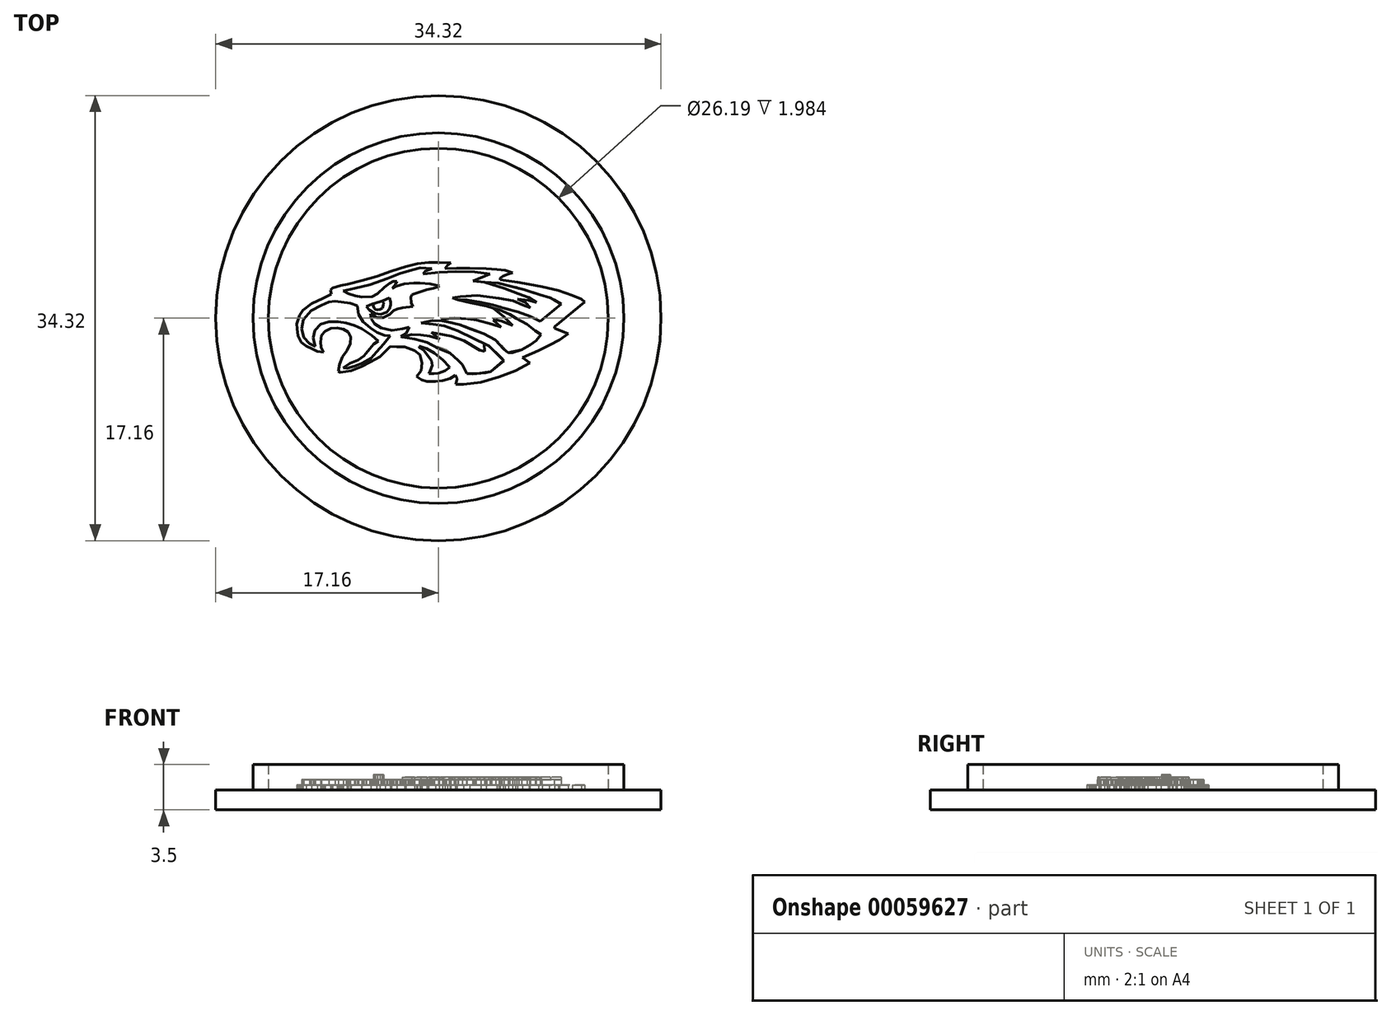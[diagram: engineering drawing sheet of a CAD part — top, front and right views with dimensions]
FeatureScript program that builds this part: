
annotation { "Feature Type Name" : "Feature", "Feature Type Description" : "" }
export const myFeature = defineFeature(function(context is Context, id is Id, definition is map)
    precondition{}
    {
        {
            var Q0;
            Q0=qCreatedBy(makeId("Top.planeOp"),FACE);
            var sketch = newSketch(context, id + "F0", { "sketchPlane" : qUnion([Q0])});
            skCircle(sketch, "E0", {"center": v(0, 0) * mm, "radius": 13.1 * mm});
            skSolve(sketch);
        }
        {
            var Q0;
            Q0=makeQuery(id+"F0.imprint","IMPRINT",FACE,{"disambiguationData":[TD([[makeQuery(id+"F0.imprint","IMPRINT",EDGE,{"derivedFrom":sQuery(id+"F0.wireOp",EDGE,"E0")}),1.0]])]});
            var sketch = newSketch(context, id + "F1", { "sketchPlane" : qUnion([Q0])});
            skLineSegment(sketch, "E1", {"start": v(-8.25, 1.86) * mm, "end": v(-8.31, 2.16) * mm});
            skLineSegment(sketch, "E2", {"start": v(-8.31, 2.16) * mm, "end": v(-8.17, 2.34) * mm});
            skLineSegment(sketch, "E3", {"start": v(-8.17, 2.34) * mm, "end": v(-7.5, 2.52) * mm});
            skLineSegment(sketch, "E4", {"start": v(-7.5, 2.52) * mm, "end": v(-7.03, 2.61) * mm});
            skLineSegment(sketch, "E5", {"start": v(-7.03, 2.61) * mm, "end": v(-5.88, 2.9) * mm});
            skLineSegment(sketch, "E6", {"start": v(-5.88, 2.9) * mm, "end": v(-4.76, 3.23) * mm});
            skLineSegment(sketch, "E7", {"start": v(-4.76, 3.23) * mm, "end": v(-3.62, 3.64) * mm});
            skLineSegment(sketch, "E8", {"start": v(-3.62, 3.64) * mm, "end": v(-2.5, 3.98) * mm});
            skLineSegment(sketch, "E9", {"start": v(-2.5, 3.98) * mm, "end": v(-1.62, 4.19) * mm});
            skLineSegment(sketch, "E10", {"start": v(-1.62, 4.19) * mm, "end": v(-0.77, 4.29) * mm});
            skLineSegment(sketch, "E11", {"start": v(-0.77, 4.29) * mm, "end": v(0.08, 4.3) * mm});
            skLineSegment(sketch, "E12", {"start": v(0.08, 4.3) * mm, "end": v(0.97, 4.25) * mm});
            skLineSegment(sketch, "E13", {"start": v(0.97, 4.25) * mm, "end": v(0.7, 4.06) * mm});
            skLineSegment(sketch, "E14", {"start": v(0.7, 4.06) * mm, "end": v(0.52, 3.84) * mm});
            skLineSegment(sketch, "E15", {"start": v(1.4, 3.85) * mm, "end": v(0.52, 3.84) * mm});
            skLineSegment(sketch, "E16", {"start": v(2.43, 3.85) * mm, "end": v(1.4, 3.85) * mm});
            skLineSegment(sketch, "E17", {"start": v(2.43, 3.85) * mm, "end": v(3.68, 3.82) * mm});
            skLineSegment(sketch, "E18", {"start": v(3.68, 3.82) * mm, "end": v(4.52, 3.76) * mm});
            skLineSegment(sketch, "E19", {"start": v(4.52, 3.76) * mm, "end": v(5.15, 3.7) * mm});
            skLineSegment(sketch, "E20", {"start": v(5.15, 3.7) * mm, "end": v(5.73, 3.51) * mm});
            skLineSegment(sketch, "E21", {"start": v(5.73, 3.51) * mm, "end": v(5.42, 3.4) * mm});
            skLineSegment(sketch, "E22", {"start": v(5.42, 3.4) * mm, "end": v(4.99, 3.26) * mm});
            skLineSegment(sketch, "E23", {"start": v(4.99, 3.26) * mm, "end": v(4.78, 3.1) * mm});
            skLineSegment(sketch, "E24", {"start": v(4.78, 3.1) * mm, "end": v(4.76, 2.97) * mm});
            skLineSegment(sketch, "E25", {"start": v(4.76, 2.97) * mm, "end": v(6.1, 2.76) * mm});
            skLineSegment(sketch, "E26", {"start": v(6.1, 2.76) * mm, "end": v(6.98, 2.63) * mm});
            skLineSegment(sketch, "E27", {"start": v(6.98, 2.63) * mm, "end": v(8, 2.44) * mm});
            skLineSegment(sketch, "E28", {"start": v(8, 2.44) * mm, "end": v(9.23, 2.15) * mm});
            skLineSegment(sketch, "E29", {"start": v(9.23, 2.15) * mm, "end": v(10.32, 1.76) * mm});
            skLineSegment(sketch, "E30", {"start": v(10.32, 1.76) * mm, "end": v(11.02, 1.46) * mm});
            skLineSegment(sketch, "E31", {"start": v(11.02, 1.46) * mm, "end": v(11.27, 1.26) * mm});
            skLineSegment(sketch, "E32", {"start": v(11.27, 1.26) * mm, "end": v(8.96, -0.67) * mm});
            skLineSegment(sketch, "E33", {"start": v(8.96, -0.67) * mm, "end": v(8.96, -0.78) * mm});
            skLineSegment(sketch, "E34", {"start": v(8.96, -0.78) * mm, "end": v(10, -1.18) * mm});
            skLineSegment(sketch, "E35", {"start": v(10, -1.18) * mm, "end": v(9.34, -1.68) * mm});
            skLineSegment(sketch, "E36", {"start": v(9.34, -1.68) * mm, "end": v(8.56, -2.1) * mm});
            skLineSegment(sketch, "E37", {"start": v(8.56, -2.1) * mm, "end": v(7.72, -2.5) * mm});
            skLineSegment(sketch, "E38", {"start": v(7.72, -2.5) * mm, "end": v(6.48, -3.05) * mm});
            skLineSegment(sketch, "E39", {"start": v(6.48, -3.05) * mm, "end": v(7.04, -3.45) * mm});
            skLineSegment(sketch, "E40", {"start": v(7.04, -3.45) * mm, "end": v(5.93, -4.04) * mm});
            skLineSegment(sketch, "E41", {"start": v(5.93, -4.04) * mm, "end": v(4.68, -4.54) * mm});
            skLineSegment(sketch, "E42", {"start": v(4.68, -4.54) * mm, "end": v(3.27, -4.94) * mm});
            skLineSegment(sketch, "E43", {"start": v(3.27, -4.94) * mm, "end": v(1.95, -5.1) * mm});
            skLineSegment(sketch, "E44", {"start": v(1.95, -5.1) * mm, "end": v(1.35, -5.1) * mm});
            skLineSegment(sketch, "E45", {"start": v(1.35, -5.1) * mm, "end": v(1.45, -4.73) * mm});
            skLineSegment(sketch, "E46", {"start": v(1.45, -4.73) * mm, "end": v(1.4, -4.53) * mm});
            skLineSegment(sketch, "E47", {"start": v(1.4, -4.53) * mm, "end": v(1.3, -4.41) * mm});
            skLineSegment(sketch, "E48", {"start": v(1.3, -4.41) * mm, "end": v(0.9, -4.65) * mm});
            skLineSegment(sketch, "E49", {"start": v(0.9, -4.65) * mm, "end": v(0.32, -4.83) * mm});
            skLineSegment(sketch, "E50", {"start": v(0.32, -4.83) * mm, "end": v(-0.22, -4.88) * mm});
            skLineSegment(sketch, "E51", {"start": v(-0.22, -4.88) * mm, "end": v(-0.88, -4.86) * mm});
            skLineSegment(sketch, "E52", {"start": v(-0.88, -4.86) * mm, "end": v(-1.29, -4.75) * mm});
            skLineSegment(sketch, "E53", {"start": v(-1.29, -4.75) * mm, "end": v(-1.67, -4.5) * mm});
            skLineSegment(sketch, "E54", {"start": v(-1.67, -4.5) * mm, "end": v(-1.33, -4.06) * mm});
            skLineSegment(sketch, "E55", {"start": v(-1.33, -4.06) * mm, "end": v(-1.25, -3.45) * mm});
            skLineSegment(sketch, "E56", {"start": v(-1.25, -3.45) * mm, "end": v(-1.43, -2.82) * mm});
            skLineSegment(sketch, "E57", {"start": v(-1.43, -2.82) * mm, "end": v(-1.83, -2.5) * mm});
            skLineSegment(sketch, "E58", {"start": v(-1.83, -2.5) * mm, "end": v(-2.59, -2.2) * mm});
            skLineSegment(sketch, "E59", {"start": v(-2.59, -2.2) * mm, "end": v(-3.2, -2.23) * mm});
            skLineSegment(sketch, "E60", {"start": v(-3.2, -2.23) * mm, "end": v(-3.71, -2.18) * mm});
            skLineSegment(sketch, "E61", {"start": v(-3.71, -2.18) * mm, "end": v(-4.08, -2.56) * mm});
            skLineSegment(sketch, "E62", {"start": v(-4.08, -2.56) * mm, "end": v(-4.52, -2.97) * mm});
            skLineSegment(sketch, "E63", {"start": v(-4.52, -2.97) * mm, "end": v(-5.2, -3.37) * mm});
            skLineSegment(sketch, "E64", {"start": v(-5.2, -3.37) * mm, "end": v(-5.93, -3.74) * mm});
            skLineSegment(sketch, "E65", {"start": v(-5.93, -3.74) * mm, "end": v(-6.74, -4.06) * mm});
            skLineSegment(sketch, "E66", {"start": v(-6.74, -4.06) * mm, "end": v(-7.54, -4.19) * mm});
            skLineSegment(sketch, "E67", {"start": v(-7.54, -4.19) * mm, "end": v(-7.72, -4.07) * mm});
            skLineSegment(sketch, "E68", {"start": v(-7.72, -4.07) * mm, "end": v(-7.6, -3.54) * mm});
            skLineSegment(sketch, "E69", {"start": v(-7.6, -3.54) * mm, "end": v(-7.4, -2.97) * mm});
            skLineSegment(sketch, "E70", {"start": v(-7.4, -2.97) * mm, "end": v(-7.04, -2.48) * mm});
            skLineSegment(sketch, "E71", {"start": v(-7.04, -2.48) * mm, "end": v(-6.78, -1.95) * mm});
            skLineSegment(sketch, "E72", {"start": v(-6.78, -1.95) * mm, "end": v(-6.77, -1.45) * mm});
            skLineSegment(sketch, "E73", {"start": v(-6.77, -1.45) * mm, "end": v(-6.95, -1.08) * mm});
            skLineSegment(sketch, "E74", {"start": v(-6.95, -1.08) * mm, "end": v(-7.32, -0.86) * mm});
            skLineSegment(sketch, "E75", {"start": v(-7.32, -0.86) * mm, "end": v(-7.8, -0.75) * mm});
            skLineSegment(sketch, "E76", {"start": v(-7.8, -0.75) * mm, "end": v(-8.28, -0.8) * mm});
            skLineSegment(sketch, "E77", {"start": v(-8.28, -0.8) * mm, "end": v(-8.73, -1) * mm});
            skLineSegment(sketch, "E78", {"start": v(-8.73, -1) * mm, "end": v(-9, -1.33) * mm});
            skLineSegment(sketch, "E79", {"start": v(-9, -1.33) * mm, "end": v(-9.08, -1.82) * mm});
            skLineSegment(sketch, "E80", {"start": v(-9.08, -1.82) * mm, "end": v(-9.04, -2.24) * mm});
            skLineSegment(sketch, "E81", {"start": v(-9.04, -2.24) * mm, "end": v(-8.84, -2.61) * mm});
            skLineSegment(sketch, "E82", {"start": v(-8.84, -2.61) * mm, "end": v(-9.32, -2.55) * mm});
            skLineSegment(sketch, "E83", {"start": v(-9.32, -2.55) * mm, "end": v(-9.71, -2.37) * mm});
            skLineSegment(sketch, "E84", {"start": v(-9.71, -2.37) * mm, "end": v(-10.18, -2.16) * mm});
            skLineSegment(sketch, "E85", {"start": v(-10.18, -2.16) * mm, "end": v(-10.58, -1.87) * mm});
            skLineSegment(sketch, "E86", {"start": v(-10.58, -1.87) * mm, "end": v(-10.82, -1.36) * mm});
            skLineSegment(sketch, "E87", {"start": v(-10.82, -1.36) * mm, "end": v(-10.9, -0.83) * mm});
            skLineSegment(sketch, "E88", {"start": v(-10.9, -0.83) * mm, "end": v(-10.92, -0.42) * mm});
            skLineSegment(sketch, "E89", {"start": v(-10.92, -0.42) * mm, "end": v(-10.7, 0.22) * mm});
            skLineSegment(sketch, "E90", {"start": v(-10.7, 0.22) * mm, "end": v(-10.43, 0.6) * mm});
            skLineSegment(sketch, "E91", {"start": v(-10.43, 0.6) * mm, "end": v(-9.76, 1.13) * mm});
            skLineSegment(sketch, "E92", {"start": v(-9.76, 1.13) * mm, "end": v(-8.9, 1.52) * mm});
            skLineSegment(sketch, "E93", {"start": v(-8.9, 1.52) * mm, "end": v(-8.25, 1.86) * mm});
            skSolve(sketch);
        }
        {
            var Q0;
            Q0 = qSketchRegion(id + "F1", true);
            extrude(context, id + "F2", {"entities" : qUnion([Q0]), "depth" : 0.4 * mm});
        }
        {
            var Q0;
            Q0=makeQuery(id+"F2.opExtrude","CAP_FACE",FACE,{"disambiguationData":[OSD([sQuery(id+"F1.wireOp",EDGE,"E1"),sQuery(id+"F1.wireOp",EDGE,"E2"),sQuery(id+"F1.wireOp",EDGE,"E3"),sQuery(id+"F1.wireOp",EDGE,"E4"),sQuery(id+"F1.wireOp",EDGE,"E5"),sQuery(id+"F1.wireOp",EDGE,"E6"),sQuery(id+"F1.wireOp",EDGE,"E7"),sQuery(id+"F1.wireOp",EDGE,"E8"),sQuery(id+"F1.wireOp",EDGE,"E9"),sQuery(id+"F1.wireOp",EDGE,"E10"),sQuery(id+"F1.wireOp",EDGE,"E11"),sQuery(id+"F1.wireOp",EDGE,"E12"),sQuery(id+"F1.wireOp",EDGE,"E13"),sQuery(id+"F1.wireOp",EDGE,"E14"),sQuery(id+"F1.wireOp",EDGE,"E15"),sQuery(id+"F1.wireOp",EDGE,"E16"),sQuery(id+"F1.wireOp",EDGE,"E17"),sQuery(id+"F1.wireOp",EDGE,"E18"),sQuery(id+"F1.wireOp",EDGE,"E19"),sQuery(id+"F1.wireOp",EDGE,"E20"),sQuery(id+"F1.wireOp",EDGE,"E21"),sQuery(id+"F1.wireOp",EDGE,"E22"),sQuery(id+"F1.wireOp",EDGE,"E23"),sQuery(id+"F1.wireOp",EDGE,"E24"),sQuery(id+"F1.wireOp",EDGE,"E25"),sQuery(id+"F1.wireOp",EDGE,"E26"),sQuery(id+"F1.wireOp",EDGE,"E27"),sQuery(id+"F1.wireOp",EDGE,"E28"),sQuery(id+"F1.wireOp",EDGE,"E29"),sQuery(id+"F1.wireOp",EDGE,"E30"),sQuery(id+"F1.wireOp",EDGE,"E31"),sQuery(id+"F1.wireOp",EDGE,"E32"),sQuery(id+"F1.wireOp",EDGE,"E33"),sQuery(id+"F1.wireOp",EDGE,"E34"),sQuery(id+"F1.wireOp",EDGE,"E35"),sQuery(id+"F1.wireOp",EDGE,"E36"),sQuery(id+"F1.wireOp",EDGE,"E37"),sQuery(id+"F1.wireOp",EDGE,"E38"),sQuery(id+"F1.wireOp",EDGE,"E39"),sQuery(id+"F1.wireOp",EDGE,"E40"),sQuery(id+"F1.wireOp",EDGE,"E41"),sQuery(id+"F1.wireOp",EDGE,"E42"),sQuery(id+"F1.wireOp",EDGE,"E43"),sQuery(id+"F1.wireOp",EDGE,"E44"),sQuery(id+"F1.wireOp",EDGE,"E45"),sQuery(id+"F1.wireOp",EDGE,"E46"),sQuery(id+"F1.wireOp",EDGE,"E47"),sQuery(id+"F1.wireOp",EDGE,"E48"),sQuery(id+"F1.wireOp",EDGE,"E49"),sQuery(id+"F1.wireOp",EDGE,"E50"),sQuery(id+"F1.wireOp",EDGE,"E51"),sQuery(id+"F1.wireOp",EDGE,"E52"),sQuery(id+"F1.wireOp",EDGE,"E53"),sQuery(id+"F1.wireOp",EDGE,"E54"),sQuery(id+"F1.wireOp",EDGE,"E55"),sQuery(id+"F1.wireOp",EDGE,"E56"),sQuery(id+"F1.wireOp",EDGE,"E57"),sQuery(id+"F1.wireOp",EDGE,"E58"),sQuery(id+"F1.wireOp",EDGE,"E59"),sQuery(id+"F1.wireOp",EDGE,"E60"),sQuery(id+"F1.wireOp",EDGE,"E61"),sQuery(id+"F1.wireOp",EDGE,"E62"),sQuery(id+"F1.wireOp",EDGE,"E63"),sQuery(id+"F1.wireOp",EDGE,"E64"),sQuery(id+"F1.wireOp",EDGE,"E65"),sQuery(id+"F1.wireOp",EDGE,"E66"),sQuery(id+"F1.wireOp",EDGE,"E67"),sQuery(id+"F1.wireOp",EDGE,"E68"),sQuery(id+"F1.wireOp",EDGE,"E69"),sQuery(id+"F1.wireOp",EDGE,"E70"),sQuery(id+"F1.wireOp",EDGE,"E71"),sQuery(id+"F1.wireOp",EDGE,"E72"),sQuery(id+"F1.wireOp",EDGE,"E73"),sQuery(id+"F1.wireOp",EDGE,"E74"),sQuery(id+"F1.wireOp",EDGE,"E75"),sQuery(id+"F1.wireOp",EDGE,"E76"),sQuery(id+"F1.wireOp",EDGE,"E77"),sQuery(id+"F1.wireOp",EDGE,"E78"),sQuery(id+"F1.wireOp",EDGE,"E79"),sQuery(id+"F1.wireOp",EDGE,"E80"),sQuery(id+"F1.wireOp",EDGE,"E81"),sQuery(id+"F1.wireOp",EDGE,"E82"),sQuery(id+"F1.wireOp",EDGE,"E83"),sQuery(id+"F1.wireOp",EDGE,"E84"),sQuery(id+"F1.wireOp",EDGE,"E85"),sQuery(id+"F1.wireOp",EDGE,"E86"),sQuery(id+"F1.wireOp",EDGE,"E87"),sQuery(id+"F1.wireOp",EDGE,"E88"),sQuery(id+"F1.wireOp",EDGE,"E89"),sQuery(id+"F1.wireOp",EDGE,"E90"),sQuery(id+"F1.wireOp",EDGE,"E91"),sQuery(id+"F1.wireOp",EDGE,"E92"),sQuery(id+"F1.wireOp",EDGE,"E93")])],"isStart":false});
            var sketch = newSketch(context, id + "F3", { "sketchPlane" : qUnion([Q0])});
            skLineSegment(sketch, "E94", {"start": v(-7.32, 2.1) * mm, "end": v(-6.48, 2.29) * mm});
            skLineSegment(sketch, "E95", {"start": v(-6.48, 2.29) * mm, "end": v(-5.26, 2.57) * mm});
            skLineSegment(sketch, "E96", {"start": v(-5.26, 2.57) * mm, "end": v(-3.95, 3.07) * mm});
            skLineSegment(sketch, "E97", {"start": v(-3.95, 3.07) * mm, "end": v(-2.99, 3.44) * mm});
            skLineSegment(sketch, "E98", {"start": v(-2.99, 3.44) * mm, "end": v(-2, 3.71) * mm});
            skLineSegment(sketch, "E99", {"start": v(-2, 3.71) * mm, "end": v(-1.4, 3.9) * mm});
            skLineSegment(sketch, "E100", {"start": v(-1.4, 3.9) * mm, "end": v(-0.51, 3.81) * mm});
            skLineSegment(sketch, "E101", {"start": v(-0.51, 3.81) * mm, "end": v(-1, 3.63) * mm});
            skLineSegment(sketch, "E102", {"start": v(-1, 3.63) * mm, "end": v(-1.18, 3.42) * mm});
            skLineSegment(sketch, "E103", {"start": v(-1.18, 3.42) * mm, "end": v(0.05, 3.55) * mm});
            skLineSegment(sketch, "E104", {"start": v(0.05, 3.55) * mm, "end": v(1.33, 3.6) * mm});
            skLineSegment(sketch, "E105", {"start": v(1.33, 3.6) * mm, "end": v(2.79, 3.58) * mm});
            skLineSegment(sketch, "E106", {"start": v(2.79, 3.58) * mm, "end": v(3.97, 3.41) * mm});
            skLineSegment(sketch, "E107", {"start": v(3.97, 3.41) * mm, "end": v(2.68, 2.85) * mm});
            skLineSegment(sketch, "E108", {"start": v(2.68, 2.85) * mm, "end": v(3.57, 2.77) * mm});
            skLineSegment(sketch, "E109", {"start": v(3.57, 2.77) * mm, "end": v(4.83, 2.6) * mm});
            skLineSegment(sketch, "E110", {"start": v(4.83, 2.6) * mm, "end": v(6.03, 2.36) * mm});
            skLineSegment(sketch, "E111", {"start": v(6.03, 2.36) * mm, "end": v(7.1, 2.05) * mm});
            skLineSegment(sketch, "E112", {"start": v(7.1, 2.05) * mm, "end": v(7.96, 1.76) * mm});
            skLineSegment(sketch, "E113", {"start": v(7.96, 1.76) * mm, "end": v(8.91, 1.42) * mm});
            skLineSegment(sketch, "E114", {"start": v(8.91, 1.42) * mm, "end": v(9.48, 1.1) * mm});
            skLineSegment(sketch, "E115", {"start": v(9.48, 1.1) * mm, "end": v(7.85, -0.25) * mm});
            skLineSegment(sketch, "E116", {"start": v(7.85, -0.25) * mm, "end": v(7.03, 0.17) * mm});
            skLineSegment(sketch, "E117", {"start": v(7.03, 0.17) * mm, "end": v(5.88, 0.57) * mm});
            skLineSegment(sketch, "E118", {"start": v(5.88, 0.57) * mm, "end": v(4.83, 0.9) * mm});
            skLineSegment(sketch, "E119", {"start": v(4.83, 0.9) * mm, "end": v(3.56, 1.16) * mm});
            skLineSegment(sketch, "E120", {"start": v(3.56, 1.16) * mm, "end": v(2.72, 1.3) * mm});
            skLineSegment(sketch, "E121", {"start": v(2.72, 1.3) * mm, "end": v(2.2, 1.41) * mm});
            skLineSegment(sketch, "E122", {"start": v(2.2, 1.41) * mm, "end": v(1.52, 1.42) * mm});
            skLineSegment(sketch, "E123", {"start": v(1.52, 1.42) * mm, "end": v(2.49, 1.2) * mm});
            skLineSegment(sketch, "E124", {"start": v(2.49, 1.2) * mm, "end": v(3.72, 0.92) * mm});
            skLineSegment(sketch, "E125", {"start": v(3.72, 0.92) * mm, "end": v(4.72, 0.64) * mm});
            skLineSegment(sketch, "E126", {"start": v(4.72, 0.64) * mm, "end": v(5.5, 0.29) * mm});
            skLineSegment(sketch, "E127", {"start": v(5.5, 0.29) * mm, "end": v(6.21, -0.14) * mm});
            skLineSegment(sketch, "E128", {"start": v(6.21, -0.14) * mm, "end": v(6.82, -0.48) * mm});
            skLineSegment(sketch, "E129", {"start": v(6.82, -0.48) * mm, "end": v(7.45, -0.99) * mm});
            skLineSegment(sketch, "E130", {"start": v(7.45, -0.99) * mm, "end": v(7.9, -1.27) * mm});
            skLineSegment(sketch, "E131", {"start": v(7.9, -1.27) * mm, "end": v(7.54, -1.7) * mm});
            skLineSegment(sketch, "E132", {"start": v(7.54, -1.7) * mm, "end": v(7.08, -2.04) * mm});
            skLineSegment(sketch, "E133", {"start": v(7.08, -2.04) * mm, "end": v(6.42, -2.43) * mm});
            skLineSegment(sketch, "E134", {"start": v(6.42, -2.43) * mm, "end": v(5.72, -2.65) * mm});
            skLineSegment(sketch, "E135", {"start": v(5.72, -2.65) * mm, "end": v(5.38, -2.64) * mm});
            skLineSegment(sketch, "E136", {"start": v(5.38, -2.64) * mm, "end": v(4.68, -1.86) * mm});
            skLineSegment(sketch, "E137", {"start": v(4.68, -1.86) * mm, "end": v(4.11, -1.5) * mm});
            skLineSegment(sketch, "E138", {"start": v(4.11, -1.5) * mm, "end": v(2.89, -0.92) * mm});
            skLineSegment(sketch, "E139", {"start": v(2.89, -0.92) * mm, "end": v(2.16, -0.64) * mm});
            skLineSegment(sketch, "E140", {"start": v(2.16, -0.64) * mm, "end": v(0.95, -0.34) * mm});
            skLineSegment(sketch, "E141", {"start": v(0.95, -0.34) * mm, "end": v(0.3, -0.2) * mm});
            skLineSegment(sketch, "E142", {"start": v(0.3, -0.2) * mm, "end": v(-0.44, -0.19) * mm});
            skLineSegment(sketch, "E143", {"start": v(-0.44, -0.19) * mm, "end": v(-1.33, -0.36) * mm});
            skLineSegment(sketch, "E144", {"start": v(-1.33, -0.36) * mm, "end": v(-0.42, -0.46) * mm});
            skLineSegment(sketch, "E145", {"start": v(-0.42, -0.46) * mm, "end": v(0.45, -0.59) * mm});
            skLineSegment(sketch, "E146", {"start": v(0.45, -0.59) * mm, "end": v(1.5, -0.98) * mm});
            skLineSegment(sketch, "E147", {"start": v(1.5, -0.98) * mm, "end": v(2.74, -1.58) * mm});
            skLineSegment(sketch, "E148", {"start": v(2.74, -1.58) * mm, "end": v(3.74, -2.07) * mm});
            skLineSegment(sketch, "E149", {"start": v(3.74, -2.07) * mm, "end": v(4.43, -2.63) * mm});
            skLineSegment(sketch, "E150", {"start": v(4.43, -2.63) * mm, "end": v(4.89, -3.1) * mm});
            skLineSegment(sketch, "E151", {"start": v(4.89, -3.1) * mm, "end": v(5.05, -3.28) * mm});
            skLineSegment(sketch, "E152", {"start": v(5.05, -3.28) * mm, "end": v(4.02, -4.12) * mm});
            skLineSegment(sketch, "E153", {"start": v(4.02, -4.12) * mm, "end": v(3.63, -4.2) * mm});
            skLineSegment(sketch, "E154", {"start": v(3.63, -4.2) * mm, "end": v(3.26, -4.23) * mm});
            skLineSegment(sketch, "E155", {"start": v(3.26, -4.23) * mm, "end": v(2.63, -4.3) * mm});
            skLineSegment(sketch, "E156", {"start": v(2.63, -4.3) * mm, "end": v(2.2, -4.26) * mm});
            skLineSegment(sketch, "E157", {"start": v(2.2, -4.26) * mm, "end": v(1.84, -3.58) * mm});
            skLineSegment(sketch, "E158", {"start": v(1.84, -3.58) * mm, "end": v(1.22, -2.94) * mm});
            skLineSegment(sketch, "E159", {"start": v(1.22, -2.94) * mm, "end": v(0.6, -2.45) * mm});
            skLineSegment(sketch, "E160", {"start": v(0.6, -2.45) * mm, "end": v(-1.24, -1.72) * mm});
            skLineSegment(sketch, "E161", {"start": v(-1.24, -1.72) * mm, "end": v(-1.83, -1.6) * mm});
            skLineSegment(sketch, "E162", {"start": v(-1.83, -1.6) * mm, "end": v(-2.8, -1.43) * mm});
            skLineSegment(sketch, "E163", {"start": v(-2.8, -1.43) * mm, "end": v(-2.9, -1.43) * mm});
            skLineSegment(sketch, "E164", {"start": v(-2.9, -1.43) * mm, "end": v(-2.52, -1.18) * mm});
            skLineSegment(sketch, "E165", {"start": v(-2.52, -1.18) * mm, "end": v(-2.35, -0.9) * mm});
            skLineSegment(sketch, "E166", {"start": v(-2.35, -0.9) * mm, "end": v(-2.25, -0.69) * mm});
            skLineSegment(sketch, "E167", {"start": v(-2.25, -0.69) * mm, "end": v(-2.76, -0.82) * mm});
            skLineSegment(sketch, "E168", {"start": v(-2.76, -0.82) * mm, "end": v(-3.58, -0.95) * mm});
            skLineSegment(sketch, "E169", {"start": v(-3.58, -0.95) * mm, "end": v(-4.42, -0.76) * mm});
            skLineSegment(sketch, "E170", {"start": v(-4.42, -0.76) * mm, "end": v(-4.92, -0.45) * mm});
            skLineSegment(sketch, "E171", {"start": v(-4.92, -0.45) * mm, "end": v(-5.17, -0.04) * mm});
            skLineSegment(sketch, "E172", {"start": v(-5.17, -0.04) * mm, "end": v(-5.22, 0.33) * mm});
            skLineSegment(sketch, "E173", {"start": v(-5.22, 0.33) * mm, "end": v(-4.77, 0.05) * mm});
            skLineSegment(sketch, "E174", {"start": v(-4.77, 0.05) * mm, "end": v(-4.25, 0.04) * mm});
            skLineSegment(sketch, "E175", {"start": v(-4.25, 0.04) * mm, "end": v(-3.75, 0.3) * mm});
            skLineSegment(sketch, "E176", {"start": v(-3.75, 0.3) * mm, "end": v(-3.45, 0.58) * mm});
            skLineSegment(sketch, "E177", {"start": v(-3.45, 0.58) * mm, "end": v(-3.16, 0.72) * mm});
            skLineSegment(sketch, "E178", {"start": v(-3.16, 0.72) * mm, "end": v(-2.74, 0.8) * mm});
            skLineSegment(sketch, "E179", {"start": v(-2.74, 0.8) * mm, "end": v(-1.95, 0.9) * mm});
            skLineSegment(sketch, "E180", {"start": v(-1.95, 0.9) * mm, "end": v(-2.09, 1.2) * mm});
            skLineSegment(sketch, "E181", {"start": v(-2.09, 1.2) * mm, "end": v(-2.12, 1.63) * mm});
            skLineSegment(sketch, "E182", {"start": v(-2.12, 1.63) * mm, "end": v(-2.03, 1.82) * mm});
            skLineSegment(sketch, "E183", {"start": v(-2.03, 1.82) * mm, "end": v(-1.37, 2.05) * mm});
            skLineSegment(sketch, "E184", {"start": v(-1.37, 2.05) * mm, "end": v(-0.9, 2.2) * mm});
            skLineSegment(sketch, "E185", {"start": v(-0.9, 2.2) * mm, "end": v(-0.41, 2.31) * mm});
            skLineSegment(sketch, "E186", {"start": v(-0.41, 2.31) * mm, "end": v(0, 2.42) * mm});
            skLineSegment(sketch, "E187", {"start": v(0, 2.42) * mm, "end": v(0.06, 2.48) * mm});
            skLineSegment(sketch, "E188", {"start": v(0.06, 2.48) * mm, "end": v(-0.62, 2.65) * mm});
            skLineSegment(sketch, "E189", {"start": v(-0.62, 2.65) * mm, "end": v(-1.41, 2.72) * mm});
            skLineSegment(sketch, "E190", {"start": v(-1.41, 2.72) * mm, "end": v(-1.91, 2.73) * mm});
            skLineSegment(sketch, "E191", {"start": v(-1.91, 2.73) * mm, "end": v(-2.62, 2.64) * mm});
            skLineSegment(sketch, "E192", {"start": v(-2.62, 2.64) * mm, "end": v(-3.26, 2.44) * mm});
            skLineSegment(sketch, "E193", {"start": v(-3.26, 2.44) * mm, "end": v(-3.55, 2.29) * mm});
            skLineSegment(sketch, "E194", {"start": v(-3.55, 2.29) * mm, "end": v(-3.3, 2.62) * mm});
            skLineSegment(sketch, "E195", {"start": v(-3.3, 2.62) * mm, "end": v(-3.2, 2.84) * mm});
            skLineSegment(sketch, "E196", {"start": v(-3.2, 2.84) * mm, "end": v(-3.48, 2.85) * mm});
            skLineSegment(sketch, "E197", {"start": v(-3.48, 2.85) * mm, "end": v(-3.77, 2.68) * mm});
            skLineSegment(sketch, "E198", {"start": v(-3.77, 2.68) * mm, "end": v(-4.16, 2.38) * mm});
            skLineSegment(sketch, "E199", {"start": v(-4.16, 2.38) * mm, "end": v(-4.7, 1.89) * mm});
            skLineSegment(sketch, "E200", {"start": v(-4.7, 1.89) * mm, "end": v(-5.1, 1.67) * mm});
            skLineSegment(sketch, "E201", {"start": v(-5.1, 1.67) * mm, "end": v(-5.89, 1.63) * mm});
            skLineSegment(sketch, "E202", {"start": v(-5.89, 1.63) * mm, "end": v(-6.4, 1.72) * mm});
            skLineSegment(sketch, "E203", {"start": v(-6.4, 1.72) * mm, "end": v(-6.9, 1.88) * mm});
            skLineSegment(sketch, "E204", {"start": v(-6.9, 1.88) * mm, "end": v(-7.32, 2.1) * mm});
            skSolve(sketch);
        }
        {
            var Q0;
            Q0 = qSketchRegion(id + "F3", true);
            extrude(context, id + "F4", {"entities" : qUnion([Q0]), "operationType" : NewBodyOperationType.ADD, "depth" : 0.4 * mm});
        }
        {
            var Q0;
            Q0=makeQuery(id+"F2.opExtrude","CAP_FACE",FACE,{"disambiguationData":[OSD([sQuery(id+"F1.wireOp",EDGE,"E1"),sQuery(id+"F1.wireOp",EDGE,"E2"),sQuery(id+"F1.wireOp",EDGE,"E3"),sQuery(id+"F1.wireOp",EDGE,"E4"),sQuery(id+"F1.wireOp",EDGE,"E5"),sQuery(id+"F1.wireOp",EDGE,"E6"),sQuery(id+"F1.wireOp",EDGE,"E7"),sQuery(id+"F1.wireOp",EDGE,"E8"),sQuery(id+"F1.wireOp",EDGE,"E9"),sQuery(id+"F1.wireOp",EDGE,"E10"),sQuery(id+"F1.wireOp",EDGE,"E11"),sQuery(id+"F1.wireOp",EDGE,"E12"),sQuery(id+"F1.wireOp",EDGE,"E13"),sQuery(id+"F1.wireOp",EDGE,"E14"),sQuery(id+"F1.wireOp",EDGE,"E15"),sQuery(id+"F1.wireOp",EDGE,"E16"),sQuery(id+"F1.wireOp",EDGE,"E17"),sQuery(id+"F1.wireOp",EDGE,"E18"),sQuery(id+"F1.wireOp",EDGE,"E19"),sQuery(id+"F1.wireOp",EDGE,"E20"),sQuery(id+"F1.wireOp",EDGE,"E21"),sQuery(id+"F1.wireOp",EDGE,"E22"),sQuery(id+"F1.wireOp",EDGE,"E23"),sQuery(id+"F1.wireOp",EDGE,"E24"),sQuery(id+"F1.wireOp",EDGE,"E25"),sQuery(id+"F1.wireOp",EDGE,"E26"),sQuery(id+"F1.wireOp",EDGE,"E27"),sQuery(id+"F1.wireOp",EDGE,"E28"),sQuery(id+"F1.wireOp",EDGE,"E29"),sQuery(id+"F1.wireOp",EDGE,"E30"),sQuery(id+"F1.wireOp",EDGE,"E31"),sQuery(id+"F1.wireOp",EDGE,"E32"),sQuery(id+"F1.wireOp",EDGE,"E33"),sQuery(id+"F1.wireOp",EDGE,"E34"),sQuery(id+"F1.wireOp",EDGE,"E35"),sQuery(id+"F1.wireOp",EDGE,"E36"),sQuery(id+"F1.wireOp",EDGE,"E37"),sQuery(id+"F1.wireOp",EDGE,"E38"),sQuery(id+"F1.wireOp",EDGE,"E39"),sQuery(id+"F1.wireOp",EDGE,"E40"),sQuery(id+"F1.wireOp",EDGE,"E41"),sQuery(id+"F1.wireOp",EDGE,"E42"),sQuery(id+"F1.wireOp",EDGE,"E43"),sQuery(id+"F1.wireOp",EDGE,"E44"),sQuery(id+"F1.wireOp",EDGE,"E45"),sQuery(id+"F1.wireOp",EDGE,"E46"),sQuery(id+"F1.wireOp",EDGE,"E47"),sQuery(id+"F1.wireOp",EDGE,"E48"),sQuery(id+"F1.wireOp",EDGE,"E49"),sQuery(id+"F1.wireOp",EDGE,"E50"),sQuery(id+"F1.wireOp",EDGE,"E51"),sQuery(id+"F1.wireOp",EDGE,"E52"),sQuery(id+"F1.wireOp",EDGE,"E53"),sQuery(id+"F1.wireOp",EDGE,"E54"),sQuery(id+"F1.wireOp",EDGE,"E55"),sQuery(id+"F1.wireOp",EDGE,"E56"),sQuery(id+"F1.wireOp",EDGE,"E57"),sQuery(id+"F1.wireOp",EDGE,"E58"),sQuery(id+"F1.wireOp",EDGE,"E59"),sQuery(id+"F1.wireOp",EDGE,"E60"),sQuery(id+"F1.wireOp",EDGE,"E61"),sQuery(id+"F1.wireOp",EDGE,"E62"),sQuery(id+"F1.wireOp",EDGE,"E63"),sQuery(id+"F1.wireOp",EDGE,"E64"),sQuery(id+"F1.wireOp",EDGE,"E65"),sQuery(id+"F1.wireOp",EDGE,"E66"),sQuery(id+"F1.wireOp",EDGE,"E67"),sQuery(id+"F1.wireOp",EDGE,"E68"),sQuery(id+"F1.wireOp",EDGE,"E69"),sQuery(id+"F1.wireOp",EDGE,"E70"),sQuery(id+"F1.wireOp",EDGE,"E71"),sQuery(id+"F1.wireOp",EDGE,"E72"),sQuery(id+"F1.wireOp",EDGE,"E73"),sQuery(id+"F1.wireOp",EDGE,"E74"),sQuery(id+"F1.wireOp",EDGE,"E75"),sQuery(id+"F1.wireOp",EDGE,"E76"),sQuery(id+"F1.wireOp",EDGE,"E77"),sQuery(id+"F1.wireOp",EDGE,"E78"),sQuery(id+"F1.wireOp",EDGE,"E79"),sQuery(id+"F1.wireOp",EDGE,"E80"),sQuery(id+"F1.wireOp",EDGE,"E81"),sQuery(id+"F1.wireOp",EDGE,"E82"),sQuery(id+"F1.wireOp",EDGE,"E83"),sQuery(id+"F1.wireOp",EDGE,"E84"),sQuery(id+"F1.wireOp",EDGE,"E85"),sQuery(id+"F1.wireOp",EDGE,"E86"),sQuery(id+"F1.wireOp",EDGE,"E87"),sQuery(id+"F1.wireOp",EDGE,"E88"),sQuery(id+"F1.wireOp",EDGE,"E89"),sQuery(id+"F1.wireOp",EDGE,"E90"),sQuery(id+"F1.wireOp",EDGE,"E91"),sQuery(id+"F1.wireOp",EDGE,"E92"),sQuery(id+"F1.wireOp",EDGE,"E93")])],"isStart":false});
            var sketch = newSketch(context, id + "F5", { "sketchPlane" : qUnion([Q0])});
            skLineSegment(sketch, "E205", {"start": v(-1.5, -2.14) * mm, "end": v(-0.9, -2.32) * mm});
            skLineSegment(sketch, "E206", {"start": v(-0.9, -2.32) * mm, "end": v(-0.3, -2.67) * mm});
            skLineSegment(sketch, "E207", {"start": v(-0.3, -2.67) * mm, "end": v(0.37, -3.23) * mm});
            skLineSegment(sketch, "E208", {"start": v(0.37, -3.23) * mm, "end": v(0.84, -3.72) * mm});
            skLineSegment(sketch, "E209", {"start": v(0.84, -3.72) * mm, "end": v(0.87, -3.8) * mm});
            skLineSegment(sketch, "E210", {"start": v(0.87, -3.8) * mm, "end": v(0.52, -4.05) * mm});
            skLineSegment(sketch, "E211", {"start": v(0.52, -4.05) * mm, "end": v(0, -4.24) * mm});
            skLineSegment(sketch, "E212", {"start": v(0, -4.24) * mm, "end": v(-0.33, -4.28) * mm});
            skLineSegment(sketch, "E213", {"start": v(-0.33, -4.28) * mm, "end": v(-0.72, -4.27) * mm});
            skLineSegment(sketch, "E214", {"start": v(-0.72, -4.27) * mm, "end": v(-0.62, -4.04) * mm});
            skLineSegment(sketch, "E215", {"start": v(-0.62, -4.04) * mm, "end": v(-0.47, -3.64) * mm});
            skLineSegment(sketch, "E216", {"start": v(-0.47, -3.64) * mm, "end": v(-0.54, -3.26) * mm});
            skLineSegment(sketch, "E217", {"start": v(-0.54, -3.26) * mm, "end": v(-0.85, -2.85) * mm});
            skLineSegment(sketch, "E218", {"start": v(-0.85, -2.85) * mm, "end": v(-1.12, -2.5) * mm});
            skLineSegment(sketch, "E219", {"start": v(-1.12, -2.5) * mm, "end": v(-1.4, -2.3) * mm});
            skLineSegment(sketch, "E220", {"start": v(-1.4, -2.3) * mm, "end": v(-1.5, -2.14) * mm});
            skLineSegment(sketch, "E221", {"start": v(-9.5, -2.17) * mm, "end": v(-9.92, -1.94) * mm});
            skLineSegment(sketch, "E222", {"start": v(-9.92, -1.94) * mm, "end": v(-10.36, -1.47) * mm});
            skLineSegment(sketch, "E223", {"start": v(-10.36, -1.47) * mm, "end": v(-10.53, -0.82) * mm});
            skLineSegment(sketch, "E224", {"start": v(-10.53, -0.82) * mm, "end": v(-10.42, -0.12) * mm});
            skLineSegment(sketch, "E225", {"start": v(-10.42, -0.12) * mm, "end": v(-9.8, 0.58) * mm});
            skLineSegment(sketch, "E226", {"start": v(-9.8, 0.58) * mm, "end": v(-9.01, 1) * mm});
            skLineSegment(sketch, "E227", {"start": v(-9.01, 1) * mm, "end": v(-8.45, 1.26) * mm});
            skLineSegment(sketch, "E228", {"start": v(-8.45, 1.26) * mm, "end": v(-7.96, 1.32) * mm});
            skLineSegment(sketch, "E229", {"start": v(-7.96, 1.32) * mm, "end": v(-6.78, 1.17) * mm});
            skLineSegment(sketch, "E230", {"start": v(-6.78, 1.17) * mm, "end": v(-6.26, 0.95) * mm});
            skLineSegment(sketch, "E231", {"start": v(-6.26, 0.95) * mm, "end": v(-6.14, 0.3) * mm});
            skLineSegment(sketch, "E232", {"start": v(-6.14, 0.3) * mm, "end": v(-5.8, -0.27) * mm});
            skLineSegment(sketch, "E233", {"start": v(-5.8, -0.27) * mm, "end": v(-5.25, -0.76) * mm});
            skLineSegment(sketch, "E234", {"start": v(-5.25, -0.76) * mm, "end": v(-4.72, -1.1) * mm});
            skLineSegment(sketch, "E235", {"start": v(-4.72, -1.1) * mm, "end": v(-4.14, -1.3) * mm});
            skLineSegment(sketch, "E236", {"start": v(-4.14, -1.3) * mm, "end": v(-3.71, -1.35) * mm});
            skLineSegment(sketch, "E237", {"start": v(-3.71, -1.35) * mm, "end": v(-4.22, -1.97) * mm});
            skLineSegment(sketch, "E238", {"start": v(-4.22, -1.97) * mm, "end": v(-4.76, -2.6) * mm});
            skLineSegment(sketch, "E239", {"start": v(-4.76, -2.6) * mm, "end": v(-5.22, -3.1) * mm});
            skLineSegment(sketch, "E240", {"start": v(-5.22, -3.1) * mm, "end": v(-5.8, -3.45) * mm});
            skLineSegment(sketch, "E241", {"start": v(-5.8, -3.45) * mm, "end": v(-6.48, -3.69) * mm});
            skLineSegment(sketch, "E242", {"start": v(-6.48, -3.69) * mm, "end": v(-7.04, -3.86) * mm});
            skLineSegment(sketch, "E243", {"start": v(-7.04, -3.86) * mm, "end": v(-7.33, -3.84) * mm});
            skLineSegment(sketch, "E244", {"start": v(-7.33, -3.84) * mm, "end": v(-6.81, -3.5) * mm});
            skLineSegment(sketch, "E245", {"start": v(-6.81, -3.5) * mm, "end": v(-6.19, -3.22) * mm});
            skLineSegment(sketch, "E246", {"start": v(-6.19, -3.22) * mm, "end": v(-5.73, -2.92) * mm});
            skLineSegment(sketch, "E247", {"start": v(-5.73, -2.92) * mm, "end": v(-5.6, -2.73) * mm});
            skLineSegment(sketch, "E248", {"start": v(-5.6, -2.73) * mm, "end": v(-5.3, -2.37) * mm});
            skLineSegment(sketch, "E249", {"start": v(-5.3, -2.37) * mm, "end": v(-4.99, -2) * mm});
            skLineSegment(sketch, "E250", {"start": v(-4.99, -2) * mm, "end": v(-4.63, -1.78) * mm});
            skLineSegment(sketch, "E251", {"start": v(-4.63, -1.78) * mm, "end": v(-5.14, -1.3) * mm});
            skLineSegment(sketch, "E252", {"start": v(-5.14, -1.3) * mm, "end": v(-5.88, -0.8) * mm});
            skLineSegment(sketch, "E253", {"start": v(-5.88, -0.8) * mm, "end": v(-6.46, -0.55) * mm});
            skLineSegment(sketch, "E254", {"start": v(-6.46, -0.55) * mm, "end": v(-7.11, -0.37) * mm});
            skLineSegment(sketch, "E255", {"start": v(-7.11, -0.37) * mm, "end": v(-7.72, -0.27) * mm});
            skLineSegment(sketch, "E256", {"start": v(-7.72, -0.27) * mm, "end": v(-8.45, -0.29) * mm});
            skLineSegment(sketch, "E257", {"start": v(-8.45, -0.29) * mm, "end": v(-9.07, -0.47) * mm});
            skLineSegment(sketch, "E258", {"start": v(-9.07, -0.47) * mm, "end": v(-9.51, -0.93) * mm});
            skLineSegment(sketch, "E259", {"start": v(-9.51, -0.93) * mm, "end": v(-9.65, -1.5) * mm});
            skLineSegment(sketch, "E260", {"start": v(-9.65, -1.5) * mm, "end": v(-9.54, -1.96) * mm});
            skLineSegment(sketch, "E261", {"start": v(-9.54, -1.96) * mm, "end": v(-9.5, -2.17) * mm});
            skLineSegment(sketch, "E262", {"start": v(-3.76, 1.58) * mm, "end": v(-4.3, 1.35) * mm});
            skLineSegment(sketch, "E263", {"start": v(-4.3, 1.35) * mm, "end": v(-5.28, 1.02) * mm});
            skLineSegment(sketch, "E264", {"start": v(-5.28, 1.02) * mm, "end": v(-5.54, 0.9) * mm});
            skLineSegment(sketch, "E265", {"start": v(-5.54, 0.9) * mm, "end": v(-5.3, 0.6) * mm});
            skLineSegment(sketch, "E266", {"start": v(-5.3, 0.6) * mm, "end": v(-4.88, 0.36) * mm});
            skLineSegment(sketch, "E267", {"start": v(-4.88, 0.36) * mm, "end": v(-4.43, 0.3) * mm});
            skLineSegment(sketch, "E268", {"start": v(-4.43, 0.3) * mm, "end": v(-3.99, 0.47) * mm});
            skLineSegment(sketch, "E269", {"start": v(-3.99, 0.47) * mm, "end": v(-3.78, 0.7) * mm});
            skLineSegment(sketch, "E270", {"start": v(-3.78, 0.7) * mm, "end": v(-3.67, 1.02) * mm});
            skLineSegment(sketch, "E271", {"start": v(-3.67, 1.02) * mm, "end": v(-3.67, 1.24) * mm});
            skLineSegment(sketch, "E272", {"start": v(-3.67, 1.24) * mm, "end": v(-3.76, 1.58) * mm});
            skSolve(sketch);
        }
        {
            var Q0;
            Q0 = qSketchRegion(id + "F5", true);
            extrude(context, id + "F6", {"entities" : qUnion([Q0]), "operationType" : NewBodyOperationType.ADD, "depth" : 0.4 * mm});
        }
        {
            var Q0;
            Q0=makeQuery(id+"F6.opExtrude","CAP_FACE",FACE,{"disambiguationData":[OSD([sQuery(id+"F5.wireOp",EDGE,"E221"),sQuery(id+"F5.wireOp",EDGE,"E222"),sQuery(id+"F5.wireOp",EDGE,"E223"),sQuery(id+"F5.wireOp",EDGE,"E224"),sQuery(id+"F5.wireOp",EDGE,"E225"),sQuery(id+"F5.wireOp",EDGE,"E226"),sQuery(id+"F5.wireOp",EDGE,"E227"),sQuery(id+"F5.wireOp",EDGE,"E228"),sQuery(id+"F5.wireOp",EDGE,"E229"),sQuery(id+"F5.wireOp",EDGE,"E230"),sQuery(id+"F5.wireOp",EDGE,"E231"),sQuery(id+"F5.wireOp",EDGE,"E232"),sQuery(id+"F5.wireOp",EDGE,"E233"),sQuery(id+"F5.wireOp",EDGE,"E234"),sQuery(id+"F5.wireOp",EDGE,"E235"),sQuery(id+"F5.wireOp",EDGE,"E236"),sQuery(id+"F5.wireOp",EDGE,"E237"),sQuery(id+"F5.wireOp",EDGE,"E238"),sQuery(id+"F5.wireOp",EDGE,"E239"),sQuery(id+"F5.wireOp",EDGE,"E240"),sQuery(id+"F5.wireOp",EDGE,"E241"),sQuery(id+"F5.wireOp",EDGE,"E242"),sQuery(id+"F5.wireOp",EDGE,"E243"),sQuery(id+"F5.wireOp",EDGE,"E244"),sQuery(id+"F5.wireOp",EDGE,"E245"),sQuery(id+"F5.wireOp",EDGE,"E246"),sQuery(id+"F5.wireOp",EDGE,"E247"),sQuery(id+"F5.wireOp",EDGE,"E248"),sQuery(id+"F5.wireOp",EDGE,"E249"),sQuery(id+"F5.wireOp",EDGE,"E250"),sQuery(id+"F5.wireOp",EDGE,"E251"),sQuery(id+"F5.wireOp",EDGE,"E252"),sQuery(id+"F5.wireOp",EDGE,"E253"),sQuery(id+"F5.wireOp",EDGE,"E254"),sQuery(id+"F5.wireOp",EDGE,"E255"),sQuery(id+"F5.wireOp",EDGE,"E256"),sQuery(id+"F5.wireOp",EDGE,"E257"),sQuery(id+"F5.wireOp",EDGE,"E258"),sQuery(id+"F5.wireOp",EDGE,"E259"),sQuery(id+"F5.wireOp",EDGE,"E260"),sQuery(id+"F5.wireOp",EDGE,"E261")])],"isStart":false});
            var sketch = newSketch(context, id + "F7", { "sketchPlane" : qUnion([Q0])});
            skLineSegment(sketch, "E273", {"start": v(-4.35, 1.32) * mm, "end": v(-4.22, 1.2) * mm});
            skLineSegment(sketch, "E274", {"start": v(-4.22, 1.2) * mm, "end": v(-4.24, 1) * mm});
            skLineSegment(sketch, "E275", {"start": v(-4.24, 1) * mm, "end": v(-4.31, 0.78) * mm});
            skLineSegment(sketch, "E276", {"start": v(-4.31, 0.78) * mm, "end": v(-4.5, 0.67) * mm});
            skLineSegment(sketch, "E277", {"start": v(-4.5, 0.67) * mm, "end": v(-4.7, 0.64) * mm});
            skLineSegment(sketch, "E278", {"start": v(-4.7, 0.64) * mm, "end": v(-4.85, 0.7) * mm});
            skLineSegment(sketch, "E279", {"start": v(-4.85, 0.7) * mm, "end": v(-4.95, 0.77) * mm});
            skLineSegment(sketch, "E280", {"start": v(-4.95, 0.77) * mm, "end": v(-5.01, 0.93) * mm});
            skLineSegment(sketch, "E281", {"start": v(-5.01, 0.93) * mm, "end": v(-5.02, 1.03) * mm});
            skLineSegment(sketch, "E282", {"start": v(-5.02, 1.03) * mm, "end": v(-5, 1.1) * mm});
            skLineSegment(sketch, "E283", {"start": v(-5, 1.1) * mm, "end": v(-4.35, 1.32) * mm});
            skSolve(sketch);
        }
        {
            var Q0;
            Q0 = qSketchRegion(id + "F7", true);
            extrude(context, id + "F8", {"entities" : qUnion([Q0]), "depth" : 0.4 * mm});
        }
        {
            var Q0;
            Q0=makeQuery(id+"F4.opExtrude","CAP_FACE",FACE,{"disambiguationData":[OSD([sQuery(id+"F3.wireOp",EDGE,"E94"),sQuery(id+"F3.wireOp",EDGE,"E95"),sQuery(id+"F3.wireOp",EDGE,"E96"),sQuery(id+"F3.wireOp",EDGE,"E97"),sQuery(id+"F3.wireOp",EDGE,"E98"),sQuery(id+"F3.wireOp",EDGE,"E99"),sQuery(id+"F3.wireOp",EDGE,"E100"),sQuery(id+"F3.wireOp",EDGE,"E101"),sQuery(id+"F3.wireOp",EDGE,"E102"),sQuery(id+"F3.wireOp",EDGE,"E103"),sQuery(id+"F3.wireOp",EDGE,"E104"),sQuery(id+"F3.wireOp",EDGE,"E105"),sQuery(id+"F3.wireOp",EDGE,"E106"),sQuery(id+"F3.wireOp",EDGE,"E107"),sQuery(id+"F3.wireOp",EDGE,"E108"),sQuery(id+"F3.wireOp",EDGE,"E109"),sQuery(id+"F3.wireOp",EDGE,"E110"),sQuery(id+"F3.wireOp",EDGE,"E111"),sQuery(id+"F3.wireOp",EDGE,"E112"),sQuery(id+"F3.wireOp",EDGE,"E113"),sQuery(id+"F3.wireOp",EDGE,"E114"),sQuery(id+"F3.wireOp",EDGE,"E115"),sQuery(id+"F3.wireOp",EDGE,"E116"),sQuery(id+"F3.wireOp",EDGE,"E117"),sQuery(id+"F3.wireOp",EDGE,"E118"),sQuery(id+"F3.wireOp",EDGE,"E119"),sQuery(id+"F3.wireOp",EDGE,"E120"),sQuery(id+"F3.wireOp",EDGE,"E121"),sQuery(id+"F3.wireOp",EDGE,"E122"),sQuery(id+"F3.wireOp",EDGE,"E123"),sQuery(id+"F3.wireOp",EDGE,"E124"),sQuery(id+"F3.wireOp",EDGE,"E125"),sQuery(id+"F3.wireOp",EDGE,"E126"),sQuery(id+"F3.wireOp",EDGE,"E127"),sQuery(id+"F3.wireOp",EDGE,"E128"),sQuery(id+"F3.wireOp",EDGE,"E129"),sQuery(id+"F3.wireOp",EDGE,"E130"),sQuery(id+"F3.wireOp",EDGE,"E131"),sQuery(id+"F3.wireOp",EDGE,"E132"),sQuery(id+"F3.wireOp",EDGE,"E133"),sQuery(id+"F3.wireOp",EDGE,"E134"),sQuery(id+"F3.wireOp",EDGE,"E135"),sQuery(id+"F3.wireOp",EDGE,"E136"),sQuery(id+"F3.wireOp",EDGE,"E137"),sQuery(id+"F3.wireOp",EDGE,"E138"),sQuery(id+"F3.wireOp",EDGE,"E139"),sQuery(id+"F3.wireOp",EDGE,"E140"),sQuery(id+"F3.wireOp",EDGE,"E141"),sQuery(id+"F3.wireOp",EDGE,"E142"),sQuery(id+"F3.wireOp",EDGE,"E143"),sQuery(id+"F3.wireOp",EDGE,"E144"),sQuery(id+"F3.wireOp",EDGE,"E145"),sQuery(id+"F3.wireOp",EDGE,"E146"),sQuery(id+"F3.wireOp",EDGE,"E147"),sQuery(id+"F3.wireOp",EDGE,"E148"),sQuery(id+"F3.wireOp",EDGE,"E149"),sQuery(id+"F3.wireOp",EDGE,"E150"),sQuery(id+"F3.wireOp",EDGE,"E151"),sQuery(id+"F3.wireOp",EDGE,"E152"),sQuery(id+"F3.wireOp",EDGE,"E153"),sQuery(id+"F3.wireOp",EDGE,"E154"),sQuery(id+"F3.wireOp",EDGE,"E155"),sQuery(id+"F3.wireOp",EDGE,"E156"),sQuery(id+"F3.wireOp",EDGE,"E157"),sQuery(id+"F3.wireOp",EDGE,"E158"),sQuery(id+"F3.wireOp",EDGE,"E159"),sQuery(id+"F3.wireOp",EDGE,"E160"),sQuery(id+"F3.wireOp",EDGE,"E161"),sQuery(id+"F3.wireOp",EDGE,"E162"),sQuery(id+"F3.wireOp",EDGE,"E163"),sQuery(id+"F3.wireOp",EDGE,"E164"),sQuery(id+"F3.wireOp",EDGE,"E165"),sQuery(id+"F3.wireOp",EDGE,"E166"),sQuery(id+"F3.wireOp",EDGE,"E167"),sQuery(id+"F3.wireOp",EDGE,"E168"),sQuery(id+"F3.wireOp",EDGE,"E169"),sQuery(id+"F3.wireOp",EDGE,"E170"),sQuery(id+"F3.wireOp",EDGE,"E171"),sQuery(id+"F3.wireOp",EDGE,"E172"),sQuery(id+"F3.wireOp",EDGE,"E173"),sQuery(id+"F3.wireOp",EDGE,"E174"),sQuery(id+"F3.wireOp",EDGE,"E175"),sQuery(id+"F3.wireOp",EDGE,"E176"),sQuery(id+"F3.wireOp",EDGE,"E177"),sQuery(id+"F3.wireOp",EDGE,"E178"),sQuery(id+"F3.wireOp",EDGE,"E179"),sQuery(id+"F3.wireOp",EDGE,"E180"),sQuery(id+"F3.wireOp",EDGE,"E181"),sQuery(id+"F3.wireOp",EDGE,"E182"),sQuery(id+"F3.wireOp",EDGE,"E183"),sQuery(id+"F3.wireOp",EDGE,"E184"),sQuery(id+"F3.wireOp",EDGE,"E185"),sQuery(id+"F3.wireOp",EDGE,"E186"),sQuery(id+"F3.wireOp",EDGE,"E187"),sQuery(id+"F3.wireOp",EDGE,"E188"),sQuery(id+"F3.wireOp",EDGE,"E189"),sQuery(id+"F3.wireOp",EDGE,"E190"),sQuery(id+"F3.wireOp",EDGE,"E191"),sQuery(id+"F3.wireOp",EDGE,"E192"),sQuery(id+"F3.wireOp",EDGE,"E193"),sQuery(id+"F3.wireOp",EDGE,"E194"),sQuery(id+"F3.wireOp",EDGE,"E195"),sQuery(id+"F3.wireOp",EDGE,"E196"),sQuery(id+"F3.wireOp",EDGE,"E197"),sQuery(id+"F3.wireOp",EDGE,"E198"),sQuery(id+"F3.wireOp",EDGE,"E199"),sQuery(id+"F3.wireOp",EDGE,"E200"),sQuery(id+"F3.wireOp",EDGE,"E201"),sQuery(id+"F3.wireOp",EDGE,"E202"),sQuery(id+"F3.wireOp",EDGE,"E203"),sQuery(id+"F3.wireOp",EDGE,"E204")])],"isStart":false});
            var sketch = newSketch(context, id + "F9", { "sketchPlane" : qUnion([Q0])});
            skLineSegment(sketch, "E284", {"start": v(-2.8, -1.43) * mm, "end": v(-2.07, -1.27) * mm});
            skLineSegment(sketch, "E285", {"start": v(-2.07, -1.27) * mm, "end": v(-1.34, -1.3) * mm});
            skLineSegment(sketch, "E286", {"start": v(-1.34, -1.3) * mm, "end": v(-0.66, -1.39) * mm});
            skLineSegment(sketch, "E287", {"start": v(-0.66, -1.39) * mm, "end": v(0.09, -1.61) * mm});
            skLineSegment(sketch, "E288", {"start": v(0.09, -1.61) * mm, "end": v(-0.54, -1.1) * mm});
            skLineSegment(sketch, "E289", {"start": v(-0.54, -1.1) * mm, "end": v(-0.2, -1.16) * mm});
            skLineSegment(sketch, "E290", {"start": v(-0.2, -1.16) * mm, "end": v(1, -1.38) * mm});
            skLineSegment(sketch, "E291", {"start": v(1, -1.38) * mm, "end": v(1.99, -1.72) * mm});
            skLineSegment(sketch, "E292", {"start": v(1.99, -1.72) * mm, "end": v(3.17, -2.46) * mm});
            skLineSegment(sketch, "E293", {"start": v(3.17, -2.46) * mm, "end": v(3.57, -2.55) * mm});
            skLineSegment(sketch, "E294", {"start": v(3.57, -2.55) * mm, "end": v(3.54, -2) * mm});
            skLineSegment(sketch, "E295", {"start": v(3.54, -2) * mm, "end": v(3.87, -2.1) * mm});
            skLineSegment(sketch, "E296", {"start": v(3.87, -2.1) * mm, "end": v(5.03, -3.26) * mm});
            skLineSegment(sketch, "E297", {"start": v(5.03, -3.26) * mm, "end": v(4.02, -4.12) * mm});
            skLineSegment(sketch, "E298", {"start": v(4.02, -4.12) * mm, "end": v(2.95, -4.27) * mm});
            skLineSegment(sketch, "E299", {"start": v(2.95, -4.27) * mm, "end": v(2.2, -4.26) * mm});
            skLineSegment(sketch, "E300", {"start": v(2.2, -4.26) * mm, "end": v(1.84, -3.58) * mm});
            skLineSegment(sketch, "E301", {"start": v(1.84, -3.58) * mm, "end": v(1.53, -3.26) * mm});
            skLineSegment(sketch, "E302", {"start": v(1.53, -3.26) * mm, "end": v(0.9, -2.7) * mm});
            skLineSegment(sketch, "E303", {"start": v(0.9, -2.7) * mm, "end": v(0, -2.33) * mm});
            skLineSegment(sketch, "E304", {"start": v(0, -2.33) * mm, "end": v(-0.9, -1.86) * mm});
            skLineSegment(sketch, "E305", {"start": v(-0.9, -1.86) * mm, "end": v(-1.83, -1.6) * mm});
            skLineSegment(sketch, "E306", {"start": v(-1.83, -1.6) * mm, "end": v(-2.8, -1.43) * mm});
            skLineSegment(sketch, "E307", {"start": v(4.22, 0.78) * mm, "end": v(5.06, 0.11) * mm});
            skLineSegment(sketch, "E308", {"start": v(5.06, 0.11) * mm, "end": v(5.72, -0.57) * mm});
            skLineSegment(sketch, "E309", {"start": v(5.72, -0.57) * mm, "end": v(4.84, -0.2) * mm});
            skLineSegment(sketch, "E310", {"start": v(4.84, -0.2) * mm, "end": v(4.4, -0.12) * mm});
            skLineSegment(sketch, "E311", {"start": v(4.4, -0.12) * mm, "end": v(4.23, -0.14) * mm});
            skLineSegment(sketch, "E312", {"start": v(4.23, -0.14) * mm, "end": v(4.82, -0.67) * mm});
            skLineSegment(sketch, "E313", {"start": v(4.82, -0.67) * mm, "end": v(4.15, -0.45) * mm});
            skLineSegment(sketch, "E314", {"start": v(4.15, -0.45) * mm, "end": v(2.97, -0.14) * mm});
            skLineSegment(sketch, "E315", {"start": v(2.97, -0.14) * mm, "end": v(2.26, -0.05) * mm});
            skLineSegment(sketch, "E316", {"start": v(2.26, -0.05) * mm, "end": v(1.23, 0) * mm});
            skLineSegment(sketch, "E317", {"start": v(1.23, 0) * mm, "end": v(0.4, -0.06) * mm});
            skLineSegment(sketch, "E318", {"start": v(0.4, -0.06) * mm, "end": v(0.26, -0.14) * mm});
            skLineSegment(sketch, "E319", {"start": v(0.8, -0.3) * mm, "end": v(1.63, -0.49) * mm});
            skPoint(sketch, "E319.endSnap0", {"position": v(1.56, -0.49) * mm});
            skLineSegment(sketch, "E320", {"start": v(1.63, -0.49) * mm, "end": v(2.53, -0.84) * mm});
            skPoint(sketch, "E320.endSnap0", {"position": v(2.53, -0.78) * mm});
            skLineSegment(sketch, "E321", {"start": v(2.53, -0.84) * mm, "end": v(3.5, -1.2) * mm});
            skLineSegment(sketch, "E322", {"start": v(3.5, -1.2) * mm, "end": v(4.4, -1.67) * mm});
            skLineSegment(sketch, "E323", {"start": v(4.4, -1.67) * mm, "end": v(5.03, -2.38) * mm});
            skPoint(sketch, "E323.endSnap0", {"position": v(5.03, -2.25) * mm});
            skLineSegment(sketch, "E324", {"start": v(5.03, -2.38) * mm, "end": v(5.38, -2.64) * mm});
            skLineSegment(sketch, "E325", {"start": v(5.38, -2.64) * mm, "end": v(6.42, -2.43) * mm});
            skLineSegment(sketch, "E326", {"start": v(6.42, -2.43) * mm, "end": v(7.08, -2.04) * mm});
            skLineSegment(sketch, "E327", {"start": v(7.08, -2.04) * mm, "end": v(7.53, -1.73) * mm});
            skLineSegment(sketch, "E328", {"start": v(7.53, -1.73) * mm, "end": v(7.9, -1.27) * mm});
            skLineSegment(sketch, "E329", {"start": v(7.9, -1.27) * mm, "end": v(7.45, -0.99) * mm});
            skLineSegment(sketch, "E330", {"start": v(7.45, -0.99) * mm, "end": v(6.82, -0.48) * mm});
            skLineSegment(sketch, "E331", {"start": v(6.82, -0.48) * mm, "end": v(6, -0.01) * mm});
            skLineSegment(sketch, "E332", {"start": v(6, -0.01) * mm, "end": v(5.5, 0.29) * mm});
            skLineSegment(sketch, "E333", {"start": v(5.5, 0.29) * mm, "end": v(4.72, 0.64) * mm});
            skLineSegment(sketch, "E334", {"start": v(4.72, 0.64) * mm, "end": v(4.22, 0.78) * mm});
            skLineSegment(sketch, "E335", {"start": v(3.57, 2.77) * mm, "end": v(5.08, 2.3) * mm});
            skLineSegment(sketch, "E336", {"start": v(5.08, 2.3) * mm, "end": v(6.18, 1.9) * mm});
            skLineSegment(sketch, "E337", {"start": v(6.18, 1.9) * mm, "end": v(6.96, 1.61) * mm});
            skLineSegment(sketch, "E338", {"start": v(6.96, 1.61) * mm, "end": v(7.56, 1.23) * mm});
            skLineSegment(sketch, "E339", {"start": v(7.56, 1.23) * mm, "end": v(6.96, 1.38) * mm});
            skLineSegment(sketch, "E340", {"start": v(6.96, 1.38) * mm, "end": v(6.11, 1.47) * mm});
            skLineSegment(sketch, "E341", {"start": v(6.11, 1.47) * mm, "end": v(6.7, 1.23) * mm});
            skLineSegment(sketch, "E342", {"start": v(6.7, 1.23) * mm, "end": v(7.1, 0.8) * mm});
            skLineSegment(sketch, "E343", {"start": v(7.1, 0.8) * mm, "end": v(6.5, 1.03) * mm});
            skLineSegment(sketch, "E344", {"start": v(6.5, 1.03) * mm, "end": v(5.75, 1.36) * mm});
            skLineSegment(sketch, "E345", {"start": v(5.75, 1.36) * mm, "end": v(4.68, 1.54) * mm});
            skLineSegment(sketch, "E346", {"start": v(4.68, 1.54) * mm, "end": v(2.98, 1.74) * mm});
            skLineSegment(sketch, "E347", {"start": v(2.98, 1.74) * mm, "end": v(1.68, 1.65) * mm});
            skLineSegment(sketch, "E348", {"start": v(1.68, 1.65) * mm, "end": v(1.1, 1.58) * mm});
            skLineSegment(sketch, "E349", {"start": v(1.1, 1.58) * mm, "end": v(1.52, 1.42) * mm});
            skLineSegment(sketch, "E350", {"start": v(1.52, 1.42) * mm, "end": v(2.2, 1.41) * mm});
            skLineSegment(sketch, "E351", {"start": v(2.2, 1.41) * mm, "end": v(3.14, 1.23) * mm});
            skLineSegment(sketch, "E352", {"start": v(3.14, 1.23) * mm, "end": v(4.2, 1.03) * mm});
            skLineSegment(sketch, "E353", {"start": v(4.2, 1.03) * mm, "end": v(5.15, 0.74) * mm});
            skPoint(sketch, "E353.endSnap0", {"position": v(5.36, 0.74) * mm});
            skLineSegment(sketch, "E354", {"start": v(5.15, 0.74) * mm, "end": v(6.14, 0.48) * mm});
            skLineSegment(sketch, "E355", {"start": v(6.14, 0.48) * mm, "end": v(7.1, 0.13) * mm});
            skLineSegment(sketch, "E356", {"start": v(7.1, 0.13) * mm, "end": v(7.85, -0.25) * mm});
            skLineSegment(sketch, "E357", {"start": v(7.85, -0.25) * mm, "end": v(9.48, 1.1) * mm});
            skLineSegment(sketch, "E358", {"start": v(9.48, 1.1) * mm, "end": v(8.64, 1.57) * mm});
            skLineSegment(sketch, "E359", {"start": v(8.64, 1.57) * mm, "end": v(7.8, 1.82) * mm});
            skLineSegment(sketch, "E360", {"start": v(7.8, 1.82) * mm, "end": v(6.6, 2.2) * mm});
            skLineSegment(sketch, "E361", {"start": v(6.6, 2.2) * mm, "end": v(5.48, 2.5) * mm});
            skLineSegment(sketch, "E362", {"start": v(5.48, 2.5) * mm, "end": v(4.62, 2.7) * mm});
            skLineSegment(sketch, "E363", {"start": v(4.62, 2.7) * mm, "end": v(3.57, 2.77) * mm});
            skLineSegment(sketch, "E364", {"start": v(0.8, -0.3) * mm, "end": v(0.26, -0.14) * mm});
            skSolve(sketch);
        }
        {
            var Q0;
            Q0 = qSketchRegion(id + "F9", true);
            extrude(context, id + "F10", {"entities" : qUnion([Q0]), "operationType" : NewBodyOperationType.ADD, "depth" : 0.2 * mm});
        }
        {
            var Q0;
            Q0=makeQuery(id+"F0.imprint","IMPRINT",FACE,{"disambiguationData":[TD([[makeQuery(id+"F0.imprint","IMPRINT",EDGE,{"derivedFrom":sQuery(id+"F0.wireOp",EDGE,"E0")}),1.0]])]});
            var sketch = newSketch(context, id + "F11", { "sketchPlane" : qUnion([Q0])});
            skCircle(sketch, "E365", {"center": v(0, 0) * mm, "radius": 13.1 * mm});
            skCircle(sketch, "E366", {"center": v(0, 0) * mm, "radius": 14.29 * mm});
            skSolve(sketch);
        }
        {
            var Q0;
            Q0=makeQuery(id+"F11.imprint","IMPRINT",FACE,{"disambiguationData":[TD([[makeQuery(id+"F11.imprint","IMPRINT",EDGE,{"derivedFrom":sQuery(id+"F11.wireOp",EDGE,"E366")}),1.0]])]});
            var Q1;
            Q1=sQuery(id+"F11.wireOp",EDGE,"E366");
            var Q2;
            Q2=sQuery(id+"F0.wireOp",EDGE,"E0");
            extrude(context, id + "F12", {"entities" : qUnion([Q0]), "surfaceEntities" : qUnion([Q1, Q2]), "depth" : 1.98 * mm});
        }
        {
            var Q0;
            Q0=makeQuery(id+"F12.opExtrude","CAP_FACE",FACE,{"disambiguationData":[OSD([sQuery(id+"F0.wireOp",EDGE,"E0"),sQuery(id+"F11.wireOp",EDGE,"E366")])],"isStart":true});
            var sketch = newSketch(context, id + "F13", { "sketchPlane" : qUnion([Q0])});
            skCircle(sketch, "E367", {"center": v(0, 0) * mm, "radius": 17.16 * mm});
            skSolve(sketch);
        }
        {
            var Q0;
            Q0 = qSketchRegion(id + "F13", true);
            extrude(context, id + "F14", {"entities" : qUnion([Q0]), "depth" : 1.52 * mm});
        }
    });
